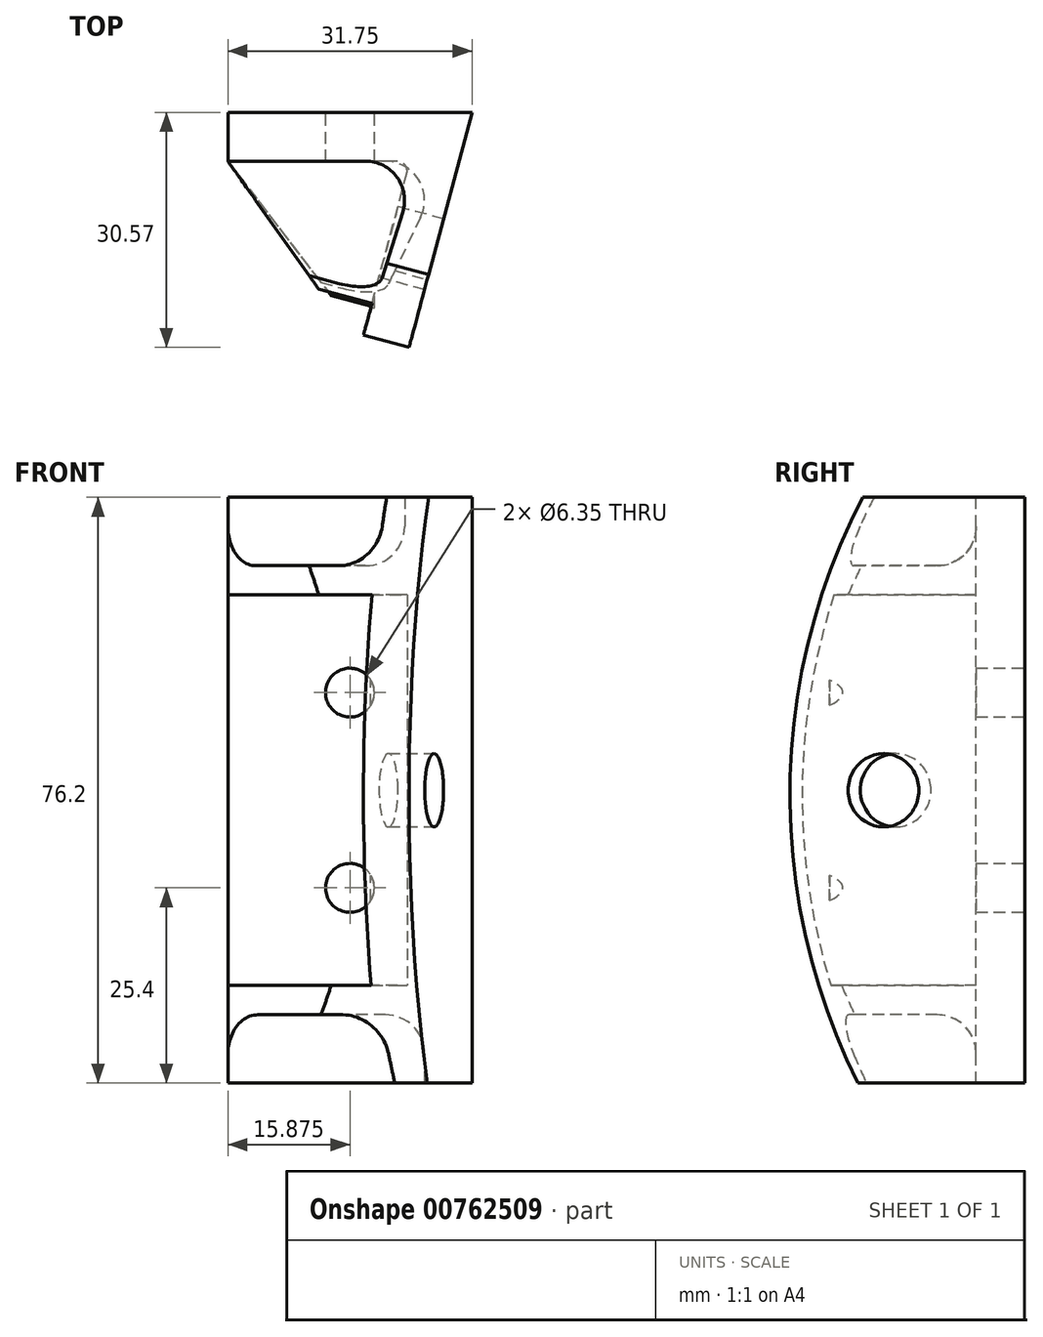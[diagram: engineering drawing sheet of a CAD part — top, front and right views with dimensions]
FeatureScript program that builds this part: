
annotation { "Feature Type Name" : "Feature", "Feature Type Description" : "" }
export const myFeature = defineFeature(function(context is Context, id is Id, definition is map)
    precondition{}
    {
        {
            var Q0;
            Q0=qCreatedBy(makeId("Top.planeOp"),FACE);
            var sketch = newSketch(context, id + "F0", { "sketchPlane" : qUnion([Q0])});
            skLineSegment(sketch, "E0", {"start": v(0, 0) * mm, "end": v(0, 6.35) * mm});
            skLineSegment(sketch, "E1", {"start": v(0, 6.35) * mm, "end": v(31.75, 6.35) * mm});
            skLineSegment(sketch, "E2", {"start": v(23.7, 0) * mm, "end": v(0, 0) * mm});
            skLineSegment(sketch, "E3", {"start": v(31.75, 6.35) * mm, "end": v(23.53, -24.32) * mm});
            skLineSegment(sketch, "E4", {"start": v(23.53, -24.32) * mm, "end": v(17.18, -24.32) * mm});
            skLineSegment(sketch, "E5", {"start": v(17.18, -24.32) * mm, "end": v(23.7, 0) * mm});
            skSolve(sketch);
        }
        {
            var Q0;
            Q0 = qSketchRegion(id + "F0", true);
            extrude(context, id + "F1", {"entities" : qUnion([Q0]), "oppositeDirection" : true, "depth" : 76.2 * mm, "offsetDistance" : 25.4 * mm});
        }
        {
            var Q0;
            Q0=makeQuery(id+"F1.opExtrude","SWEPT_FACE",FACE,{"disambiguationData":[OSD([sQuery(id+"F0.wireOp",EDGE,"E3")])]});
            var sketch = newSketch(context, id + "F2", { "sketchPlane" : qUnion([Q0])});
            skArc(sketch, "E6", {"start": v(-7.48, 0) * mm, "mid": v(-17.3, -38.02) * mm, "end": v(-8.14, -76.2) * mm});
            skLineSegment(sketch, "E7", {"start": v(-7.48, 0) * mm, "end": v(-19.04, 0) * mm});
            skLineSegment(sketch, "E8", {"start": v(-19.04, 0) * mm, "end": v(-19.04, -76.2) * mm});
            skLineSegment(sketch, "E9", {"start": v(-19.04, -76.2) * mm, "end": v(-8.14, -76.2) * mm});
            skSolve(sketch);
        }
        {
            var Q0;
            Q0=makeQuery(id+"F1.opExtrude","SWEPT_FACE",FACE,{"disambiguationData":[OSD([sQuery(id+"F0.wireOp",EDGE,"E1")])]});
            var sketch = newSketch(context, id + "F3", { "sketchPlane" : qUnion([Q0])});
            skCircle(sketch, "E10", {"center": v(-15.88, -25.4) * mm, "radius": 3.18 * mm});
            skCircle(sketch, "E11", {"center": v(-15.88, -50.8) * mm, "radius": 3.18 * mm});
            skSolve(sketch);
        }
        {
            var Q0;
            Q0 = qSketchRegion(id + "F3", true);
            extrude(context, id + "F4", {"entities" : qUnion([Q0]), "operationType" : NewBodyOperationType.REMOVE, "oppositeDirection" : true, "depth" : 25.4 * mm, "offsetDistance" : 25.4 * mm});
        }
        {
            var Q0;
            Q0=makeQuery(id+"F1.opExtrude","SWEPT_FACE",FACE,{"disambiguationData":[OSD([sQuery(id+"F0.wireOp",EDGE,"E3")])]});
            var sketch = newSketch(context, id + "F5", { "sketchPlane" : qUnion([Q0])});
            skCircle(sketch, "E12", {"center": v(-4.7, -38.1) * mm, "radius": 4.76 * mm});
            skSolve(sketch);
        }
        {
            var Q0;
            Q0=makeQuery(id+"F5.imprint","IMPRINT",FACE,{"disambiguationData":[TD([[makeQuery(id+"F5.imprint","IMPRINT",EDGE,{"derivedFrom":sQuery(id+"F5.wireOp",EDGE,"E12")}),1.0]])]});
            extrude(context, id + "F6", {"entities" : qUnion([Q0]), "operationType" : NewBodyOperationType.REMOVE, "oppositeDirection" : true, "depth" : 8.9 * mm, "offsetDistance" : 25.4 * mm});
        }
        {
            var Q0;
            Q0=makeQuery(id+"F1.opExtrude","SWEPT_EDGE",EDGE,{"disambiguationData":[OSD([sQuery(id+"F0.wireOp",EDGE,"E2"),sQuery(id+"F0.wireOp",EDGE,"E5")])]});
            fillet(context, id + "F7", {"entities" : qUnion([Q0]), "radius" : 1.27 * mm, "tangentPropagation" : true, "allowEdgeOverflow" : false});
        }
        {
            var Q0;
            Q0=makeQuery(id+"F1.opExtrude","CAP_FACE",FACE,{"disambiguationData":[OSD([sQuery(id+"F0.wireOp",EDGE,"E0"),sQuery(id+"F0.wireOp",EDGE,"E1"),sQuery(id+"F0.wireOp",EDGE,"E2"),sQuery(id+"F0.wireOp",EDGE,"E3"),sQuery(id+"F0.wireOp",EDGE,"E4"),sQuery(id+"F0.wireOp",EDGE,"E5")])],"isStart":true});
            var sketch = newSketch(context, id + "F8", { "sketchPlane" : qUnion([Q0])});
            skLineSegment(sketch, "E13", {"start": v(0, 0) * mm, "end": v(17.2, -24.23) * mm});
            skLineSegment(sketch, "E14", {"start": v(17.2, -24.23) * mm, "end": v(24.83, 0) * mm});
            skLineSegment(sketch, "E15", {"start": v(24.83, 0) * mm, "end": v(0, 0) * mm});
            skSolve(sketch);
        }
        {
            var Q0;
            {var subQ6=sQuery(id+"F8.wireOp",EDGE,"E13");Q0=makeQuery(id+"F8.imprint","IMPRINT",FACE,{"disambiguationData":[TD([[makeQuery(id+"F8.imprint","IMPRINT",EDGE,{"derivedFrom":subQ6}),1.0]])]});}
            extrude(context, id + "F9", {"entities" : qUnion([Q0]), "operationType" : NewBodyOperationType.ADD, "oppositeDirection" : true, "depth" : 12.7 * mm, "offsetDistance" : 25.4 * mm});
        }
        {
            var Q0;
            Q0 = qSketchRegion(id + "F8", true);
            extrude(context, id + "F10", {"entities" : qUnion([Q0]), "operationType" : NewBodyOperationType.REMOVE, "oppositeDirection" : true, "depth" : 8.9 * mm, "offsetDistance" : 25.4 * mm});
        }
        {
            var Q0;
            Q0=makeQuery(id+"F1.opExtrude","CAP_FACE",FACE,{"disambiguationData":[OSD([sQuery(id+"F0.wireOp",EDGE,"E0"),sQuery(id+"F0.wireOp",EDGE,"E1"),sQuery(id+"F0.wireOp",EDGE,"E2"),sQuery(id+"F0.wireOp",EDGE,"E3"),sQuery(id+"F0.wireOp",EDGE,"E4"),sQuery(id+"F0.wireOp",EDGE,"E5")])],"isStart":false});
            var sketch = newSketch(context, id + "F11", { "sketchPlane" : qUnion([Q0])});
            skLineSegment(sketch, "E16", {"start": v(0, 0) * mm, "end": v(28.58, 0) * mm});
            skLineSegment(sketch, "E17", {"start": v(0, 0) * mm, "end": v(17.57, 22.89) * mm});
            skLineSegment(sketch, "E18", {"start": v(28.58, 0) * mm, "end": v(17.57, 22.89) * mm});
            skSolve(sketch);
        }
        {
            var Q0;
            Q0 = qSketchRegion(id + "F11", true);
            extrude(context, id + "F12", {"entities" : qUnion([Q0]), "operationType" : NewBodyOperationType.ADD, "oppositeDirection" : true, "depth" : 12.7 * mm, "offsetDistance" : 25.4 * mm});
        }
        {
            var Q0;
            Q0 = qSketchRegion(id + "F2", true);
            extrude(context, id + "F13", {"entities" : qUnion([Q0]), "operationType" : NewBodyOperationType.REMOVE, "oppositeDirection" : true, "depth" : 52.83 * mm, "offsetDistance" : 25.4 * mm});
        }
        {
            var Q0;
            Q0 = qSketchRegion(id + "F11", true);
            extrude(context, id + "F14", {"entities" : qUnion([Q0]), "operationType" : NewBodyOperationType.REMOVE, "oppositeDirection" : true, "depth" : 8.9 * mm, "offsetDistance" : 25.4 * mm});
        }
        {
            var Q0;
            Q0=makeQuery(id+"F10.boolean.opBoolean","COPY",EDGE,{"derivedFrom":makeQuery(id+"F10.opExtrude","CAP_EDGE",EDGE,{"disambiguationData":[OSD([sQuery(id+"F8.wireOp",EDGE,"E14")])],"isStart":false})});
            var Q1;
            Q1=makeQuery(id+"F10.boolean.opBoolean","COPY",EDGE,{"derivedFrom":makeQuery(id+"F10.opExtrude","CAP_EDGE",EDGE,{"disambiguationData":[OSD([sQuery(id+"F8.wireOp",EDGE,"E15")])],"isStart":false})});
            var Q2;
            Q2=makeQuery(id+"F10.boolean.opBoolean","COPY",EDGE,{"derivedFrom":makeQuery(id+"F10.opExtrude","SWEPT_EDGE",EDGE,{"disambiguationData":[OSD([sQuery(id+"F8.wireOp",EDGE,"E14"),sQuery(id+"F8.wireOp",EDGE,"E15")])]})});
            var Q3;
            Q3=makeQuery(id+"F9.opExtrude","CAP_EDGE",EDGE,{"disambiguationData":[OSD([sQuery(id+"F0.wireOp",EDGE,"E5")])],"isStart":false});
            var Q4;
            Q4=makeQuery(id+"F14.boolean.opBoolean","COPY",EDGE,{"derivedFrom":makeQuery(id+"F14.opExtrude","CAP_EDGE",EDGE,{"disambiguationData":[OSD([sQuery(id+"F11.wireOp",EDGE,"E16")])],"isStart":false})});
            var Q5;
            Q5=makeQuery(id+"F14.boolean.opBoolean","COPY",EDGE,{"derivedFrom":makeQuery(id+"F14.opExtrude","CAP_EDGE",EDGE,{"disambiguationData":[OSD([sQuery(id+"F11.wireOp",EDGE,"E18")])],"isStart":false})});
            var Q6;
            Q6=makeQuery(id+"F12.opExtrude","CAP_EDGE",EDGE,{"disambiguationData":[OSD([sQuery(id+"F11.wireOp",EDGE,"E16")])],"isStart":false});
            var Q7;
            Q7=makeQuery(id+"F14.boolean.opBoolean","COPY",EDGE,{"derivedFrom":makeQuery(id+"F14.opExtrude","SWEPT_EDGE",EDGE,{"disambiguationData":[OSD([sQuery(id+"F11.wireOp",EDGE,"E16"),sQuery(id+"F11.wireOp",EDGE,"E18")])]})});
            fillet(context, id + "F15", {"entities" : qUnion([Q0, Q1, Q2, Q3, Q4, Q5, Q6, Q7]), "radius" : 5.08 * mm, "tangentPropagation" : true, "allowEdgeOverflow" : false});
        }
    });
